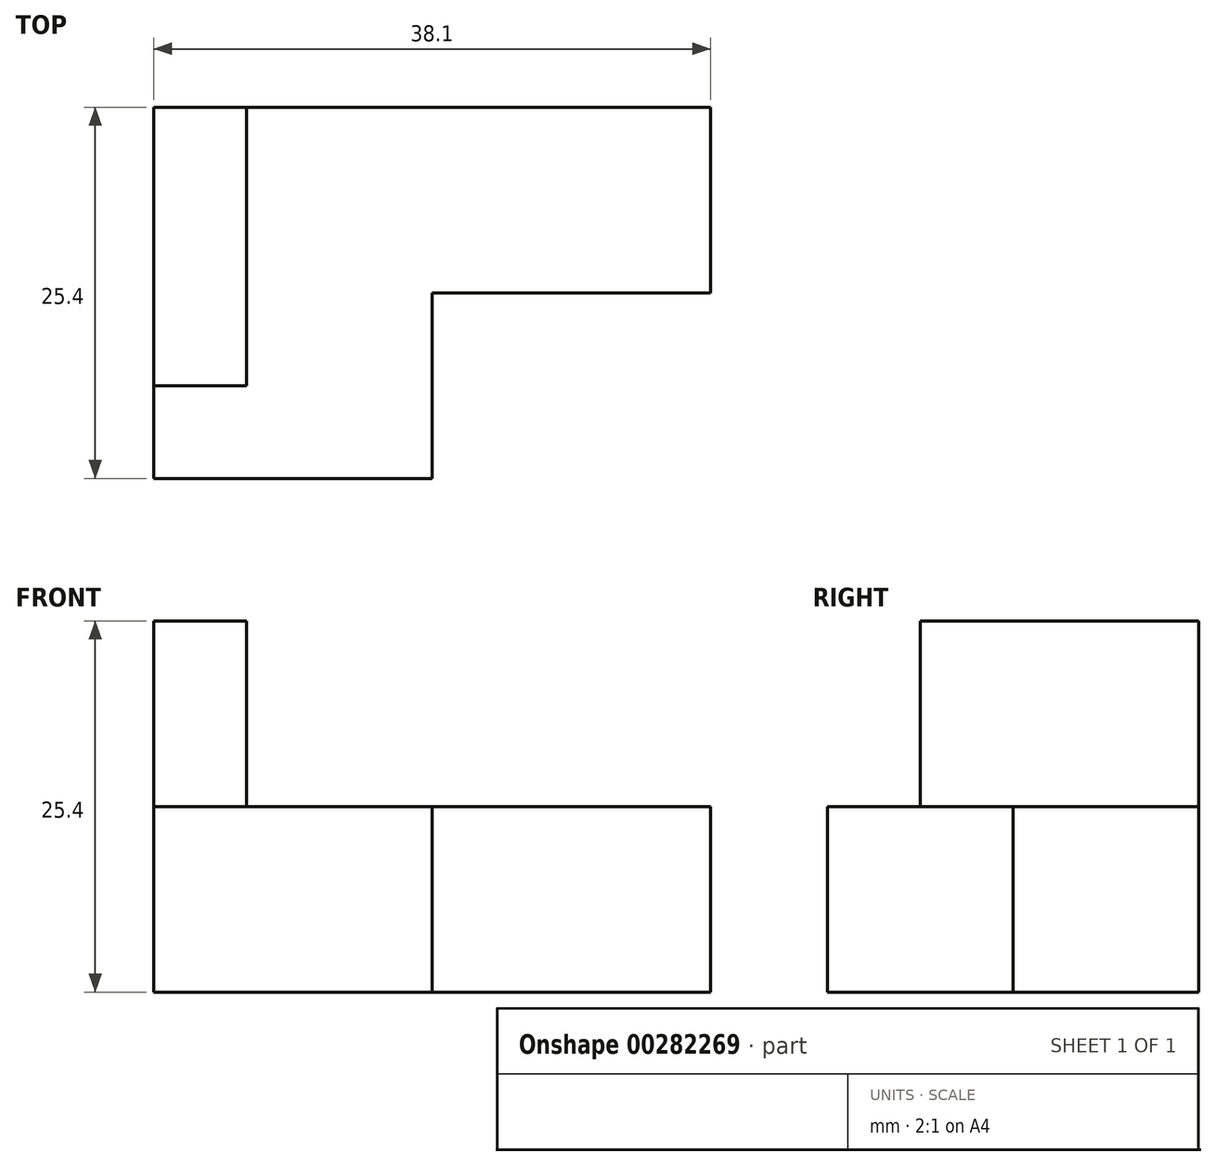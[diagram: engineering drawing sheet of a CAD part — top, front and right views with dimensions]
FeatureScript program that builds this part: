
annotation { "Feature Type Name" : "Feature", "Feature Type Description" : "" }
export const myFeature = defineFeature(function(context is Context, id is Id, definition is map)
    precondition{}
    {
        {
            var Q0;
            Q0=qCreatedBy(makeId("Top.planeOp"),FACE);
            var sketch = newSketch(context, id + "F0", { "sketchPlane" : qUnion([Q0])});
            skLineSegment(sketch, "E0", {"start": v(0, 0) * mm, "end": v(0, -12.7) * mm});
            skLineSegment(sketch, "E1", {"start": v(0, -12.7) * mm, "end": v(19.05, -12.7) * mm});
            skLineSegment(sketch, "E2", {"start": v(19.05, -12.7) * mm, "end": v(19.05, 0) * mm});
            skLineSegment(sketch, "E3", {"start": v(19.05, 0) * mm, "end": v(38.1, 0) * mm});
            skLineSegment(sketch, "E4", {"start": v(38.1, 0) * mm, "end": v(38.1, 12.7) * mm});
            skLineSegment(sketch, "E5", {"start": v(38.1, 12.7) * mm, "end": v(0, 12.7) * mm});
            skLineSegment(sketch, "E6", {"start": v(0, 12.7) * mm, "end": v(0, 0) * mm});
            skSolve(sketch);
        }
        {
            var Q0;
            Q0 = qSketchRegion(id + "F0", true);
            extrude(context, id + "F1", {"entities" : qUnion([Q0]), "depth" : 12.7 * mm});
        }
        {
            var Q0;
            Q0=makeQuery(id+"F1.opExtrude","CAP_FACE",FACE,{"disambiguationData":[OSD([sQuery(id+"F0.wireOp",EDGE,"E0"),sQuery(id+"F0.wireOp",EDGE,"E1"),sQuery(id+"F0.wireOp",EDGE,"E2"),sQuery(id+"F0.wireOp",EDGE,"E3"),sQuery(id+"F0.wireOp",EDGE,"E4"),sQuery(id+"F0.wireOp",EDGE,"E5"),sQuery(id+"F0.wireOp",EDGE,"E6")])],"isStart":false});
            var sketch = newSketch(context, id + "F2", { "sketchPlane" : qUnion([Q0])});
            skLineSegment(sketch, "E7.bottom", {"start": v(0, -6.35) * mm, "end": v(6.35, -6.35) * mm});
            skLineSegment(sketch, "E7.top", {"start": v(0, 12.7) * mm, "end": v(6.35, 12.7) * mm});
            skLineSegment(sketch, "E7.left", {"start": v(0, -6.35) * mm, "end": v(0, 12.7) * mm});
            skLineSegment(sketch, "E7.right", {"start": v(6.35, -6.35) * mm, "end": v(6.35, 12.7) * mm});
            skSolve(sketch);
        }
        {
            var Q0;
            Q0 = qSketchRegion(id + "F2", true);
            extrude(context, id + "F3", {"entities" : qUnion([Q0]), "operationType" : NewBodyOperationType.ADD, "depth" : 12.7 * mm});
        }
    });
